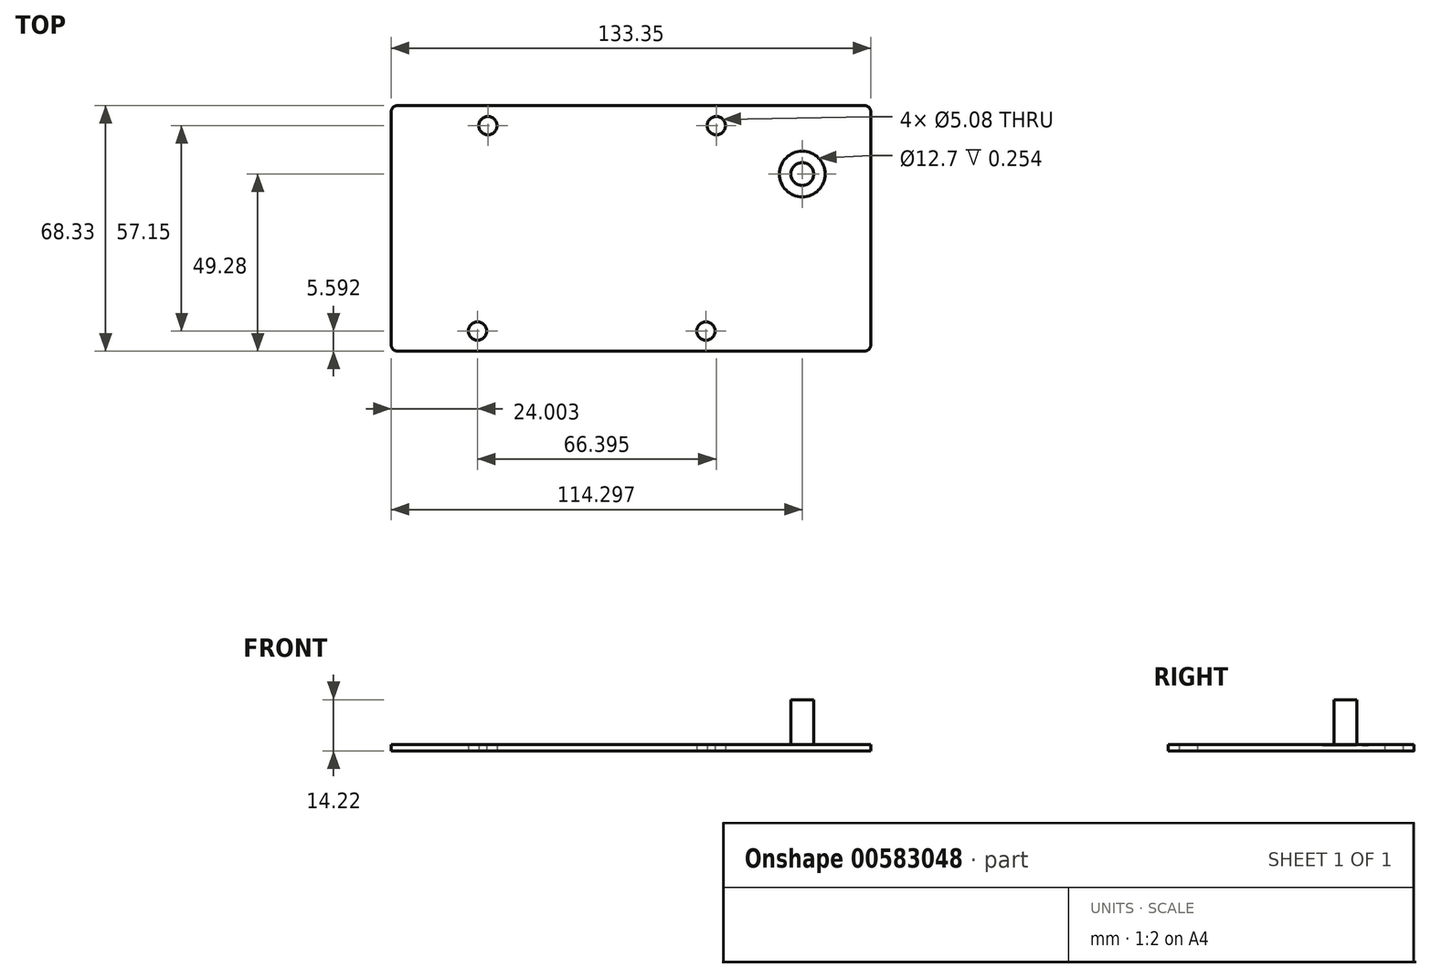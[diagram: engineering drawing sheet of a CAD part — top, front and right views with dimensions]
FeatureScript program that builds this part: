
annotation { "Feature Type Name" : "Feature", "Feature Type Description" : "" }
export const myFeature = defineFeature(function(context is Context, id is Id, definition is map)
    precondition{}
    {
        {
            var Q0;
            Q0=qCreatedBy(makeId("Top.planeOp"),FACE);
            var sketch = newSketch(context, id + "F0", { "sketchPlane" : qUnion([Q0])});
            skLineSegment(sketch, "E0.bottom", {"start": v(-16.6, -14.23) * mm, "end": v(113.19, -14.23) * mm});
            skLineSegment(sketch, "E0.top", {"start": v(-16.6, 54.1) * mm, "end": v(113.19, 54.1) * mm});
            skLineSegment(sketch, "E0.left", {"start": v(-18.38, -12.45) * mm, "end": v(-18.38, 52.32) * mm});
            skLineSegment(sketch, "E0.right", {"start": v(114.97, -12.45) * mm, "end": v(114.97, 52.32) * mm});
            skPoint(sketch, "E1.visualSharp", {"position": v(114.97, 54.1) * mm});
            skArc(sketch, "E1.filletArc", {"start": v(114.97, 52.32) * mm, "mid": v(114.45, 53.58) * mm, "end": v(113.19, 54.1) * mm});
            skPoint(sketch, "E2.visualSharp", {"position": v(114.97, -14.23) * mm});
            skArc(sketch, "E2.filletArc", {"start": v(113.19, -14.23) * mm, "mid": v(114.45, -13.7) * mm, "end": v(114.97, -12.45) * mm});
            skPoint(sketch, "E3.visualSharp", {"position": v(-18.38, -14.23) * mm});
            skArc(sketch, "E3.filletArc", {"start": v(-18.38, -12.45) * mm, "mid": v(-17.86, -13.7) * mm, "end": v(-16.6, -14.23) * mm});
            skPoint(sketch, "E4.visualSharp", {"position": v(-18.38, 54.1) * mm});
            skArc(sketch, "E4.filletArc", {"start": v(-16.6, 54.1) * mm, "mid": v(-17.86, 53.58) * mm, "end": v(-18.38, 52.32) * mm});
            skCircle(sketch, "E5", {"center": v(8.52, 48.51) * mm, "radius": 2.54 * mm});
            skCircle(sketch, "E6", {"center": v(5.62, -8.64) * mm, "radius": 2.54 * mm});
            skCircle(sketch, "E7", {"center": v(72.02, 48.51) * mm, "radius": 2.54 * mm});
            skCircle(sketch, "E8", {"center": v(69.12, -8.64) * mm, "radius": 2.54 * mm});
            skSolve(sketch);
        }
        {
            var Q0;
            Q0 = qSketchRegion(id + "F0", true);
            extrude(context, id + "F1", {"entities" : qUnion([Q0]), "depth" : 1.52 * mm, "offsetDistance" : 25.4 * mm});
        }
        {
            var Q0;
            Q0=makeQuery(id+"F1.opExtrude","CAP_FACE",FACE,{"disambiguationData":[OSD([sQuery(id+"F0.wireOp",EDGE,"E0.bottom"),sQuery(id+"F0.wireOp",EDGE,"E0.top"),sQuery(id+"F0.wireOp",EDGE,"E0.left"),sQuery(id+"F0.wireOp",EDGE,"E0.right"),sQuery(id+"F0.wireOp",EDGE,"E1.filletArc"),sQuery(id+"F0.wireOp",EDGE,"E2.filletArc"),sQuery(id+"F0.wireOp",EDGE,"E3.filletArc"),sQuery(id+"F0.wireOp",EDGE,"E4.filletArc"),sQuery(id+"F0.wireOp",EDGE,"E5"),sQuery(id+"F0.wireOp",EDGE,"E6"),sQuery(id+"F0.wireOp",EDGE,"E7"),sQuery(id+"F0.wireOp",EDGE,"E8")])],"isStart":false});
            var sketch = newSketch(context, id + "F2", { "sketchPlane" : qUnion([Q0])});
            skCircle(sketch, "E9", {"center": v(95.92, 35.05) * mm, "radius": 6.35 * mm});
            skSolve(sketch);
        }
        {
            var Q0;
            Q0=makeQuery(id+"F2.imprint","IMPRINT",FACE,{"disambiguationData":[TD([[makeQuery(id+"F2.imprint","IMPRINT",EDGE,{"derivedFrom":sQuery(id+"F2.wireOp",EDGE,"E9")}),-1.0]])]});
            extrude(context, id + "F3", {"entities" : qUnion([Q0]), "operationType" : NewBodyOperationType.ADD, "depth" : 0.25 * mm, "offsetDistance" : 25.4 * mm});
        }
        {
            var Q0;
            Q0=makeQuery(id+"F1.opExtrude","CAP_FACE",FACE,{"disambiguationData":[OSD([sQuery(id+"F0.wireOp",EDGE,"E0.bottom"),sQuery(id+"F0.wireOp",EDGE,"E0.top"),sQuery(id+"F0.wireOp",EDGE,"E0.left"),sQuery(id+"F0.wireOp",EDGE,"E0.right"),sQuery(id+"F0.wireOp",EDGE,"E1.filletArc"),sQuery(id+"F0.wireOp",EDGE,"E2.filletArc"),sQuery(id+"F0.wireOp",EDGE,"E3.filletArc"),sQuery(id+"F0.wireOp",EDGE,"E4.filletArc"),sQuery(id+"F0.wireOp",EDGE,"E5"),sQuery(id+"F0.wireOp",EDGE,"E6"),sQuery(id+"F0.wireOp",EDGE,"E7"),sQuery(id+"F0.wireOp",EDGE,"E8")])],"isStart":false});
            var sketch = newSketch(context, id + "F4", { "sketchPlane" : qUnion([Q0])});
            skCircle(sketch, "E10", {"center": v(95.92, 35.05) * mm, "radius": 3.18 * mm});
            skSolve(sketch);
        }
        {
            var Q0;
            Q0=makeQuery(id+"F4.imprint","IMPRINT",FACE,{"disambiguationData":[TD([[makeQuery(id+"F4.imprint","IMPRINT",EDGE,{"derivedFrom":sQuery(id+"F4.wireOp",EDGE,"E10")}),1.0]])]});
            extrude(context, id + "F5", {"entities" : qUnion([Q0]), "operationType" : NewBodyOperationType.ADD, "depth" : 12.7 * mm, "offsetDistance" : 25.4 * mm});
        }
    });
